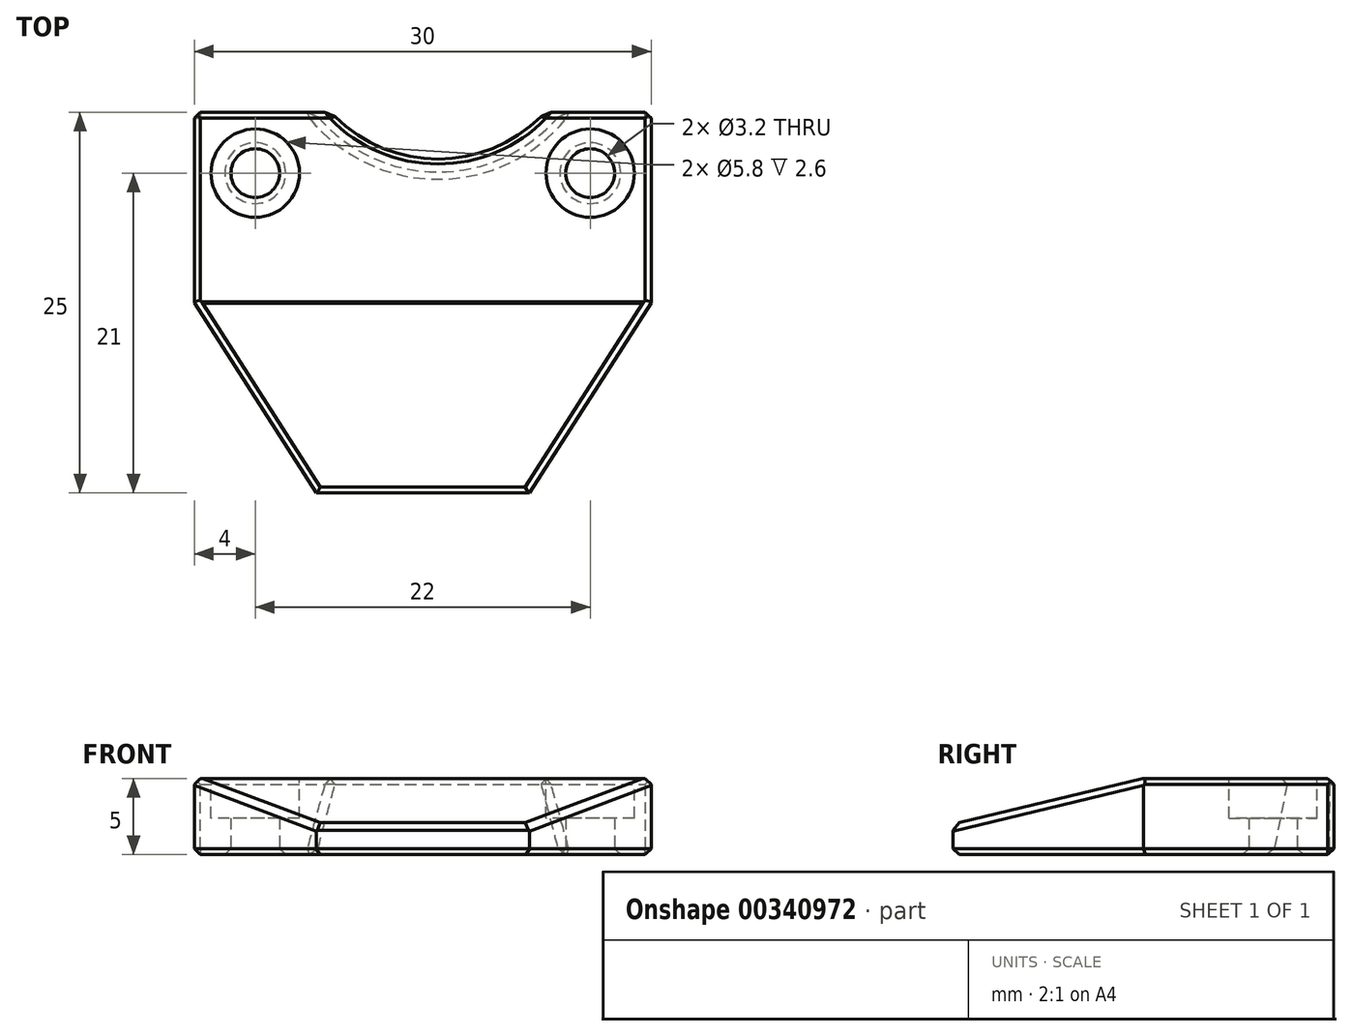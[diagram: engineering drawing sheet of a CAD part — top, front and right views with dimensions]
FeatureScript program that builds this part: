
annotation { "Feature Type Name" : "Feature", "Feature Type Description" : "" }
export const myFeature = defineFeature(function(context is Context, id is Id, definition is map)
    precondition{}
    {
        {
            var Q0;
            Q0=qCreatedBy(makeId("Top.planeOp"),FACE);
            var sketch = newSketch(context, id + "F0", { "sketchPlane" : qUnion([Q0])});
            skLineSegment(sketch, "E0.bottom", {"start": v(-15, 12.5) * mm, "end": v(-5.93, 12.5) * mm});
            skLineSegment(sketch, "E0.top", {"start": v(-7, -12.5) * mm, "end": v(7, -12.5) * mm});
            skLineSegment(sketch, "E0.left", {"start": v(-15, 12.5) * mm, "end": v(-15, 0) * mm});
            skLineSegment(sketch, "E0.right", {"start": v(15, 12.5) * mm, "end": v(15, 0) * mm});
            skPoint(sketch, "E0.middle", {"position": v(0, 0) * mm});
            skCircle(sketch, "E1", {"center": v(-11, 8.5) * mm, "radius": 1.6 * mm});
            skCircle(sketch, "E2.MirrorC", {"center": v(11, 8.5) * mm, "radius": 1.6 * mm});
            skLineSegment(sketch, "E3", {"start": v(-15, 0) * mm, "end": v(-7, -12.5) * mm});
            skLineSegment(sketch, "E4.MirrorCS", {"start": v(15, 0) * mm, "end": v(7, -12.5) * mm});
            skPoint(sketch, "E5.orphan", {"position": v(-15, -12.5) * mm});
            skPoint(sketch, "E6.orphan", {"position": v(15, -12.5) * mm});
            skArc(sketch, "E7", {"start": v(-5.93, 12.5) * mm, "mid": v(1, 9.5) * mm, "end": v(7.93, 12.5) * mm});
            skLineSegment(sketch, "E8.trimOffspring", {"start": v(7.93, 12.5) * mm, "end": v(15, 12.5) * mm});
            skSolve(sketch);
        }
        {
            var Q0;
            Q0 = qSketchRegion(id + "F0", true);
            extrude(context, id + "F1", {"entities" : qUnion([Q0]), "depth" : 5 * mm});
        }
        {
            var Q0;
            Q0=makeQuery(id+"F1.opExtrude","CAP_FACE",FACE,{"disambiguationData":[OSD([sQuery(id+"F0.wireOp",EDGE,"E0.bottom"),sQuery(id+"F0.wireOp",EDGE,"E0.top"),sQuery(id+"F0.wireOp",EDGE,"E0.left"),sQuery(id+"F0.wireOp",EDGE,"E0.right"),sQuery(id+"F0.wireOp",EDGE,"E1"),sQuery(id+"F0.wireOp",EDGE,"E2.MirrorC"),sQuery(id+"F0.wireOp",EDGE,"E3"),sQuery(id+"F0.wireOp",EDGE,"E4.MirrorCS")])],"isStart":false});
            var sketch = newSketch(context, id + "F2", { "sketchPlane" : qUnion([Q0])});
            skCircle(sketch, "E9", {"center": v(-11, 8.5) * mm, "radius": 2.9 * mm});
            skCircle(sketch, "E10.MirrorC", {"center": v(11, 8.5) * mm, "radius": 2.9 * mm});
            skSolve(sketch);
        }
        {
            var Q0;
            Q0 = qSketchRegion(id + "F2", true);
            extrude(context, id + "F3", {"entities" : qUnion([Q0]), "operationType" : NewBodyOperationType.REMOVE, "oppositeDirection" : true, "depth" : 2.6 * mm});
        }
        {
            var Q0;
            Q0=makeQuery(id+"F1.opExtrude","CAP_EDGE",EDGE,{"disambiguationData":[OSD([sQuery(id+"F0.wireOp",EDGE,"E0.top")])],"isStart":false});
            chamfer(context, id + "F4", {"entities" : qUnion([Q0]), "chamferType" : ChamferType.TWO_OFFSETS, "width1" : 12.5 * mm, "oppositeDirection" : false, "width2" : 3 * mm, "tangentPropagation" : true});
        }
        {
            var Q0;
            Q0=makeQuery(id+"F1.opExtrude","CAP_EDGE",EDGE,{"disambiguationData":[OSD([sQuery(id+"F0.wireOp",EDGE,"E7")])],"isStart":true});
            chamfer(context, id + "F5", {"entities" : qUnion([Q0]), "chamferType" : ChamferType.TWO_OFFSETS, "width1" : 1 * mm, "oppositeDirection" : false, "width2" : 5 * mm, "tangentPropagation" : true});
        }
        {
            var Q0;
            Q0=makeQuery(id+"F4.opChamfer","BLEND_FACE",FACE,{"disambiguationData":[OSD([sQuery(id+"F0.wireOp",EDGE,"E0.top")])]});
            var Q1;
            Q1=makeQuery(id+"F1.opExtrude","CAP_FACE",FACE,{"disambiguationData":[OSD([sQuery(id+"F0.wireOp",EDGE,"E0.bottom"),sQuery(id+"F0.wireOp",EDGE,"E0.top"),sQuery(id+"F0.wireOp",EDGE,"E0.left"),sQuery(id+"F0.wireOp",EDGE,"E0.right"),sQuery(id+"F0.wireOp",EDGE,"E1"),sQuery(id+"F0.wireOp",EDGE,"E2.MirrorC"),sQuery(id+"F0.wireOp",EDGE,"E3"),sQuery(id+"F0.wireOp",EDGE,"E4.MirrorCS"),sQuery(id+"F0.wireOp",EDGE,"E7"),sQuery(id+"F0.wireOp",EDGE,"E8.trimOffspring")])],"isStart":true});
            var Q2;
            Q2=makeQuery(id+"F1.opExtrude","CAP_EDGE",EDGE,{"disambiguationData":[OSD([sQuery(id+"F0.wireOp",EDGE,"E0.bottom")])],"isStart":false});
            var Q3;
            {var subQ0=sQuery(id+"F0.wireOp",EDGE,"E7");Q3=makeQuery(id+"F5.opChamfer","BLEND_EDGE",EDGE,{"blendedFrom":[makeQuery(id+"F1.opExtrude","CAP_EDGE",EDGE,{"disambiguationData":[OSD([subQ0])],"isStart":true}),makeQuery(id+"F1.opExtrude","CAP_FACE",FACE,{"disambiguationData":[OSD([sQuery(id+"F0.wireOp",EDGE,"E0.bottom"),sQuery(id+"F0.wireOp",EDGE,"E0.top"),sQuery(id+"F0.wireOp",EDGE,"E0.left"),sQuery(id+"F0.wireOp",EDGE,"E0.right"),sQuery(id+"F0.wireOp",EDGE,"E1"),sQuery(id+"F0.wireOp",EDGE,"E2.MirrorC"),sQuery(id+"F0.wireOp",EDGE,"E3"),sQuery(id+"F0.wireOp",EDGE,"E4.MirrorCS"),subQ0,sQuery(id+"F0.wireOp",EDGE,"E8.trimOffspring")])],"isStart":false})],"blendedInto":[makeQuery(id+"F1.opExtrude","CAP_FACE",FACE,{"disambiguationData":[OSD([sQuery(id+"F0.wireOp",EDGE,"E0.bottom"),sQuery(id+"F0.wireOp",EDGE,"E0.top"),sQuery(id+"F0.wireOp",EDGE,"E0.left"),sQuery(id+"F0.wireOp",EDGE,"E0.right"),sQuery(id+"F0.wireOp",EDGE,"E1"),sQuery(id+"F0.wireOp",EDGE,"E2.MirrorC"),sQuery(id+"F0.wireOp",EDGE,"E3"),sQuery(id+"F0.wireOp",EDGE,"E4.MirrorCS"),subQ0,sQuery(id+"F0.wireOp",EDGE,"E8.trimOffspring")])],"isStart":false})]});}
            var Q4;
            Q4=makeQuery(id+"F1.opExtrude","CAP_EDGE",EDGE,{"disambiguationData":[OSD([sQuery(id+"F0.wireOp",EDGE,"E8.trimOffspring")])],"isStart":false});
            var Q5;
            Q5=makeQuery(id+"F1.opExtrude","SWEPT_EDGE",EDGE,{"disambiguationData":[OSD([sQuery(id+"F0.wireOp",EDGE,"E0.right"),sQuery(id+"F0.wireOp",EDGE,"E8.trimOffspring")])]});
            var Q6;
            Q6=makeQuery(id+"F1.opExtrude","SWEPT_EDGE",EDGE,{"disambiguationData":[OSD([sQuery(id+"F0.wireOp",EDGE,"E0.bottom"),sQuery(id+"F0.wireOp",EDGE,"E0.left")])]});
            var Q7;
            Q7=makeQuery(id+"F5.opChamfer","BLEND_EDGE",EDGE,{"blendedFrom":[makeQuery(id+"F1.opExtrude","CAP_EDGE",EDGE,{"disambiguationData":[OSD([sQuery(id+"F0.wireOp",EDGE,"E7")])],"isStart":true}),makeQuery(id+"F1.opExtrude","SWEPT_FACE",FACE,{"disambiguationData":[OSD([sQuery(id+"F0.wireOp",EDGE,"E0.bottom")])]})],"blendedInto":[makeQuery(id+"F1.opExtrude","SWEPT_FACE",FACE,{"disambiguationData":[OSD([sQuery(id+"F0.wireOp",EDGE,"E0.bottom")])]})]});
            var Q8;
            Q8=makeQuery(id+"F5.opChamfer","BLEND_EDGE",EDGE,{"blendedFrom":[makeQuery(id+"F1.opExtrude","CAP_EDGE",EDGE,{"disambiguationData":[OSD([sQuery(id+"F0.wireOp",EDGE,"E7")])],"isStart":true}),makeQuery(id+"F1.opExtrude","SWEPT_FACE",FACE,{"disambiguationData":[OSD([sQuery(id+"F0.wireOp",EDGE,"E8.trimOffspring")])]})],"blendedInto":[makeQuery(id+"F1.opExtrude","SWEPT_FACE",FACE,{"disambiguationData":[OSD([sQuery(id+"F0.wireOp",EDGE,"E8.trimOffspring")])]})]});
            var Q9;
            Q9=makeQuery(id+"F3.boolean.opBoolean","COPY",EDGE,{"derivedFrom":makeQuery(id+"F3.opExtrude","CAP_EDGE",EDGE,{"disambiguationData":[OSD([sQuery(id+"F2.wireOp",EDGE,"E10.MirrorC")])],"isStart":true})});
            var Q10;
            Q10=makeQuery(id+"F3.boolean.opBoolean","COPY",EDGE,{"derivedFrom":makeQuery(id+"F3.opExtrude","CAP_EDGE",EDGE,{"disambiguationData":[OSD([sQuery(id+"F2.wireOp",EDGE,"E9")])],"isStart":true})});
            chamfer(context, id + "F6", {"entities" : qUnion([Q0, Q1, Q2, Q3, Q4, Q5, Q6, Q7, Q8, Q9, Q10]), "width" : 0.4 * mm, "tangentPropagation" : true});
        }
        {
            var Q0;
            Q0=makeQuery(id+"F1.opExtrude","CAP_EDGE",EDGE,{"disambiguationData":[OSD([sQuery(id+"F0.wireOp",EDGE,"E0.left")])],"isStart":false});
            var Q1;
            Q1=makeQuery(id+"F1.opExtrude","CAP_EDGE",EDGE,{"disambiguationData":[OSD([sQuery(id+"F0.wireOp",EDGE,"E0.right")])],"isStart":false});
            chamfer(context, id + "F7", {"entities" : qUnion([Q0, Q1]), "width" : 0.4 * mm, "tangentPropagation" : true});
        }
    });
